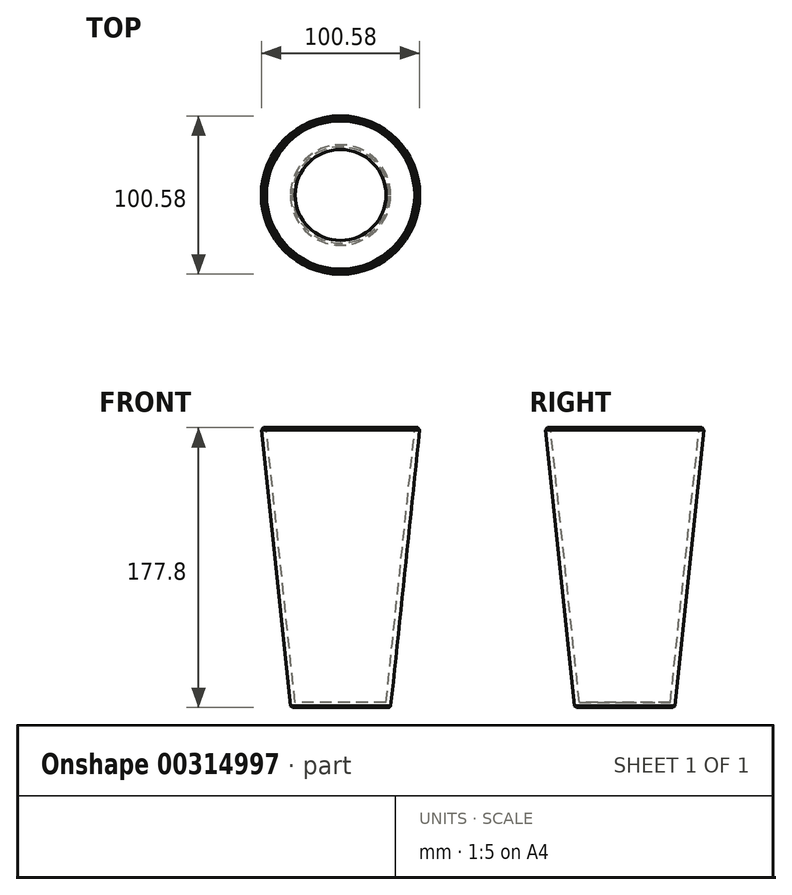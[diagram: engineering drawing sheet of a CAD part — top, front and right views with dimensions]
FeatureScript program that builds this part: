
annotation { "Feature Type Name" : "Feature", "Feature Type Description" : "" }
export const myFeature = defineFeature(function(context is Context, id is Id, definition is map)
    precondition{}
    {
        {
            var Q0;
            Q0=qCreatedBy(makeId("Top.planeOp"),FACE);
            var sketch = newSketch(context, id + "F0", { "sketchPlane" : qUnion([Q0])});
            skCircle(sketch, "E0", {"center": v(0, 0) * mm, "radius": 31.75 * mm});
            skSolve(sketch);
        }
        {
            var Q0;
            Q0 = qSketchRegion(id + "F0", true);
            extrude(context, id + "F1", {"entities" : qUnion([Q0]), "depth" : 177.8 * mm, "hasDraft" : true, "draftAngle" : 6 * degree});
        }
        {
            var Q0;
            Q0=makeQuery(id+"F1.opExtrude","CAP_FACE",FACE,{"disambiguationData":[OSD([sQuery(id+"F0.wireOp",EDGE,"E0")])],"isStart":false});
            shell(context, id + "F2", {"entities" : qUnion([Q0]), "thickness" : 3.17 * mm});
        }
        {
            var Q0;
            Q0=makeQuery(id+"F1.opExtrude","CAP_EDGE",EDGE,{"disambiguationData":[OSD([sQuery(id+"F0.wireOp",EDGE,"E0")])],"isStart":false});
            var Q1;
            {var subQ0=sQuery(id+"F0.wireOp",EDGE,"E0");Q1=makeQuery(id+"F2.opShell","OFFSET_EDGE",EDGE,{"disambiguationData":[OSD([subQ0]),TDD([makeQuery(id+"F1.opExtrude","CAP_EDGE",EDGE,{"disambiguationData":[OSD([subQ0])],"isStart":false})])]});}
            var Q2;
            Q2=makeQuery(id+"F1.opExtrude","CAP_EDGE",EDGE,{"disambiguationData":[OSD([sQuery(id+"F0.wireOp",EDGE,"E0")])],"isStart":true});
            chamfer(context, id + "F3", {"entities" : qUnion([Q0, Q1, Q2]), "width" : 1.27 * mm, "tangentPropagation" : true});
        }
    });
